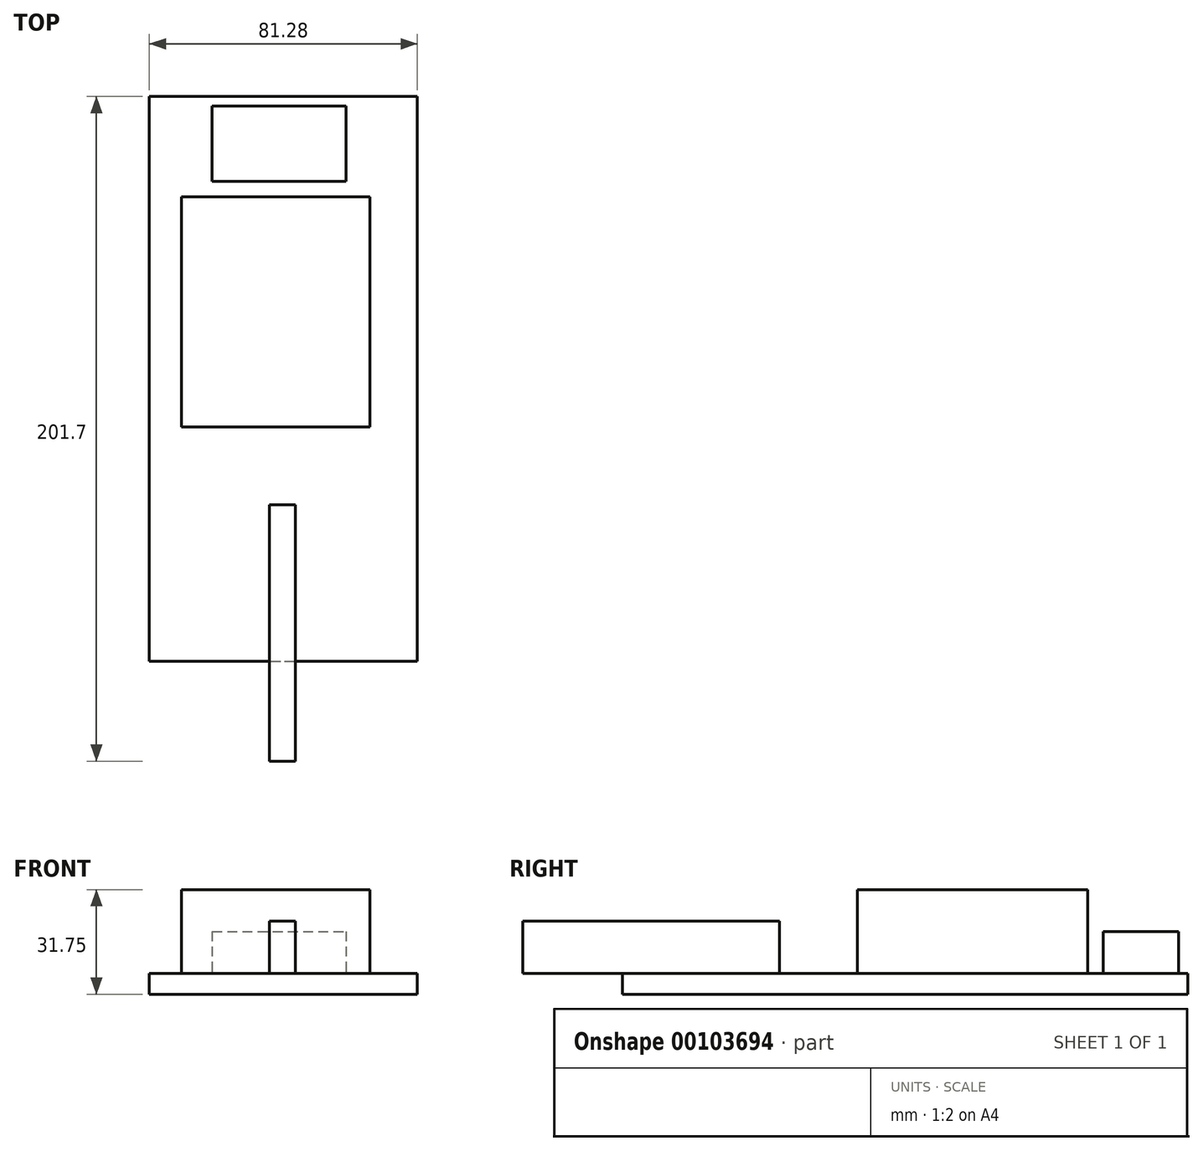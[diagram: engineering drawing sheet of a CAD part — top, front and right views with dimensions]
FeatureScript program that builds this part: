
annotation { "Feature Type Name" : "Feature", "Feature Type Description" : "" }
export const myFeature = defineFeature(function(context is Context, id is Id, definition is map)
    precondition{}
    {
        {
            var Q0;
            Q0=qCreatedBy(makeId("Top.planeOp"),FACE);
            var sketch = newSketch(context, id + "F0", { "sketchPlane" : qUnion([Q0])});
            skLineSegment(sketch, "E0.bottom", {"start": v(-88.39, 110.1) * mm, "end": v(-7.1, 110.1) * mm});
            skLineSegment(sketch, "E0.top", {"start": v(-88.39, -61.36) * mm, "end": v(-7.1, -61.36) * mm});
            skLineSegment(sketch, "E0.left", {"start": v(-88.39, 110.1) * mm, "end": v(-88.39, -61.36) * mm});
            skLineSegment(sketch, "E0.right", {"start": v(-7.1, 110.1) * mm, "end": v(-7.1, -61.36) * mm});
            skSolve(sketch);
        }
        {
            var Q0;
            Q0=makeQuery(id+"F0.imprint","IMPRINT",FACE,{"disambiguationData":[TD([[makeQuery(id+"F0.imprint","IMPRINT",EDGE,{"derivedFrom":sQuery(id+"F0.wireOp",EDGE,"E0.bottom")}),-1.0]])]});
            extrude(context, id + "F1", {"entities" : qUnion([Q0]), "depth" : 6.35 * mm});
        }
        {
            var Q0;
            Q0=makeQuery(id+"F1.opExtrude","CAP_FACE",FACE,{"disambiguationData":[OSD([sQuery(id+"F0.wireOp",EDGE,"E0.bottom"),sQuery(id+"F0.wireOp",EDGE,"E0.top"),sQuery(id+"F0.wireOp",EDGE,"E0.left"),sQuery(id+"F0.wireOp",EDGE,"E0.right")])],"isStart":false});
            var sketch = newSketch(context, id + "F2", { "sketchPlane" : qUnion([Q0])});
            skLineSegment(sketch, "E1.bottom", {"start": v(-78.57, 79.66) * mm, "end": v(-21.42, 79.66) * mm});
            skLineSegment(sketch, "E1.top", {"start": v(-78.57, 9.8) * mm, "end": v(-21.42, 9.8) * mm});
            skLineSegment(sketch, "E1.left", {"start": v(-78.57, 79.66) * mm, "end": v(-78.57, 9.8) * mm});
            skLineSegment(sketch, "E1.right", {"start": v(-21.42, 79.66) * mm, "end": v(-21.42, 9.8) * mm});
            skSolve(sketch);
        }
        {
            var Q0;
            Q0=makeQuery(id+"F2.imprint","IMPRINT",FACE,{"disambiguationData":[TD([[makeQuery(id+"F2.imprint","IMPRINT",EDGE,{"derivedFrom":sQuery(id+"F2.wireOp",EDGE,"E1.bottom")}),-1.0]])]});
            extrude(context, id + "F3", {"entities" : qUnion([Q0]), "operationType" : NewBodyOperationType.ADD, "depth" : 25.4 * mm});
        }
        {
            var Q0;
            Q0=makeQuery(id+"F1.opExtrude","CAP_FACE",FACE,{"disambiguationData":[OSD([sQuery(id+"F0.wireOp",EDGE,"E0.bottom"),sQuery(id+"F0.wireOp",EDGE,"E0.top"),sQuery(id+"F0.wireOp",EDGE,"E0.left"),sQuery(id+"F0.wireOp",EDGE,"E0.right")])],"isStart":false});
            var sketch = newSketch(context, id + "F4", { "sketchPlane" : qUnion([Q0])});
            skLineSegment(sketch, "E2.bottom", {"start": v(-69.32, 107.2) * mm, "end": v(-28.68, 107.2) * mm});
            skLineSegment(sketch, "E2.top", {"start": v(-69.32, 84.34) * mm, "end": v(-28.68, 84.34) * mm});
            skLineSegment(sketch, "E2.left", {"start": v(-69.32, 107.2) * mm, "end": v(-69.32, 84.34) * mm});
            skLineSegment(sketch, "E2.right", {"start": v(-28.68, 107.2) * mm, "end": v(-28.68, 84.34) * mm});
            skSolve(sketch);
        }
        {
            var Q0;
            Q0=makeQuery(id+"F4.imprint","IMPRINT",FACE,{"disambiguationData":[TD([[makeQuery(id+"F4.imprint","IMPRINT",EDGE,{"derivedFrom":sQuery(id+"F4.wireOp",EDGE,"E2.bottom")}),-1.0]])]});
            extrude(context, id + "F5", {"entities" : qUnion([Q0]), "operationType" : NewBodyOperationType.ADD, "depth" : 12.7 * mm});
        }
        {
            var Q0;
            Q0=makeQuery(id+"F1.opExtrude","CAP_FACE",FACE,{"disambiguationData":[OSD([sQuery(id+"F0.wireOp",EDGE,"E0.bottom"),sQuery(id+"F0.wireOp",EDGE,"E0.top"),sQuery(id+"F0.wireOp",EDGE,"E0.left"),sQuery(id+"F0.wireOp",EDGE,"E0.right")])],"isStart":false});
            var sketch = newSketch(context, id + "F6", { "sketchPlane" : qUnion([Q0])});
            skLineSegment(sketch, "E3", {"start": v(-49, 84.34) * mm, "end": v(-49, -61.36) * mm});
            skLineSegment(sketch, "E4.bottom", {"start": v(-52, -13.82) * mm, "end": v(-44.06, -13.82) * mm});
            skLineSegment(sketch, "E4.top", {"start": v(-52, -91.6) * mm, "end": v(-44.06, -91.6) * mm});
            skLineSegment(sketch, "E4.left", {"start": v(-52, -13.82) * mm, "end": v(-52, -91.6) * mm});
            skLineSegment(sketch, "E4.right", {"start": v(-44.06, -13.82) * mm, "end": v(-44.06, -91.6) * mm});
            skSolve(sketch);
        }
        {
            var Q0;
            {var subQ5=sQuery(id+"F6.wireOp",EDGE,"E4.top");Q0=makeQuery(id+"F6.imprint","IMPRINT",FACE,{"disambiguationData":[TD([[makeQuery(id+"F6.imprint","IMPRINT",EDGE,{"derivedFrom":subQ5}),1.0]])]});}
            var Q1;
            {var subQ0=sQuery(id+"F6.wireOp",EDGE,"E3");var subQ1=makeQuery(id+"F1.opExtrude","CAP_EDGE",EDGE,{"disambiguationData":[OSD([sQuery(id+"F0.wireOp",EDGE,"E0.top")])],"isStart":false});var subQ2=makeQuery(id+"F6.imprint","INTERSECT",VERTEX,{"derivedFrom":[subQ1,subQ0]});Q1=makeQuery(id+"F6.imprint","IMPRINT",FACE,{"disambiguationData":[TD([[makeQuery(id+"F6.imprint","IMPRINT",EDGE,{"disambiguationData":[TD([[subQ2,1.0]])],"derivedFrom":subQ0}),1.0]])]});}
            var Q2;
            {var subQ0=sQuery(id+"F6.wireOp",EDGE,"E3");var subQ1=makeQuery(id+"F1.opExtrude","CAP_EDGE",EDGE,{"disambiguationData":[OSD([sQuery(id+"F0.wireOp",EDGE,"E0.top")])],"isStart":false});var subQ2=makeQuery(id+"F6.imprint","INTERSECT",VERTEX,{"derivedFrom":[subQ1,subQ0]});Q2=makeQuery(id+"F6.imprint","IMPRINT",FACE,{"disambiguationData":[TD([[makeQuery(id+"F6.imprint","IMPRINT",EDGE,{"disambiguationData":[TD([[subQ2,1.0]])],"derivedFrom":subQ0}),-1.0]])]});}
            extrude(context, id + "F7", {"entities" : qUnion([Q0, Q1, Q2]), "operationType" : NewBodyOperationType.ADD, "depth" : 15.88 * mm});
        }
    });
